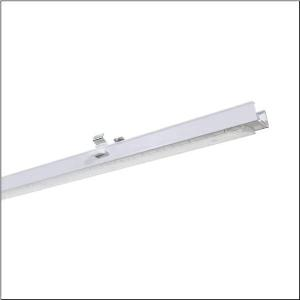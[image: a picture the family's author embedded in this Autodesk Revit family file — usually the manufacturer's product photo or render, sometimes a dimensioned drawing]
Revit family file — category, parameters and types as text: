
# Revit family: trunking_flex_31_51re19mb4cb
name_source: partatom
category: Lighting Fixtures
units: mm (PartAtom-declared; Revit-internal decimal feet)

## family parameters
Cut with Voids When Loaded = No
Host = Face
Light Source = No
Part Type = Normal
Room Calculation Point = No
Round Connector Dimension = Use Diameter
Shared = No

## types (1)
- --- (1 x LED, 11500 lm, 66 W, 4000K)
    Apparent Load = 66 VA
    CIE Flux Codes = 66 89 98 99 100
    Color Rendering = 80
    Color Temperature = 4000K
    Default Elevation = 1800 mm
    Description = Trunking Flex 31, luminaire insert, of extruded aluminium section, coated, traffic white (RAL 9016), length: 1.472mm, width: 91mm, height: 53mm, LED rated luminous flux: 11.500lm, light colour: 840, control gear: ON/OFF Multilumen, with system connector: socket, mains connection: 220..240V, AC, 50/60Hz, rated input power: 66W, connected load according to luminous flux setting (19/24/32/37/47/52/60/66W), luminous flux adjustable on luminaire in eight steps (3450/4380/5800/6700/8350/9200/10500/11500lm ), primary light control with lens, of plastic, primary optical cover: cover, of PMMA, light emission: direct distribution, primary light characteristic: double asymmetric, protection rating (complete): IP20, insulation class (complete): insulation class I (protective earthing), certification: CE, UKCA, impact resistance: IK02, permissible ambient temperature for indoor applications: -20..+40°C, packaging unit: 1 piece
    Height = 58 mm
    Lamp = 1 x LED
    Lamp Light Flux = 11500 lm
    Lamp Power = 66 W
    Lamp count = 1
    Length = 1472 mm
    Luminous efficacy = 174 lm/W
    Manufacturer = Siteco
    ModVariant = No
    Model = 51RE19MB4CB
    Mounting Place = Ceiling
    Mounting Type = Pendant
    Number of Poles = 1
    OnlyDefault = Yes
    Power Factor = 1
    Product Name = Trunking Flex 31
    Product group = luminaire insert
    ProductGroupID = 901
    Protection Class = Protection class I
    Protection Degree = IP 20
    RLX_Detail_Level = 1
    RLX_Emergency_Light_Flux = 0 lm
    RLX_Emergency_Type = 0
    RLX_Emergency_Type_DB = No
    RlxData = <blob elided: 21165 chars, md5=249072ce>
    Socket = socket
    Standby Power = 0 W
    System Light Flux = 11500 lm
    System Power = 66 W
    Type Comments = factory setting: luminous flux: 100 % | (ON | ON | ON)
    Type Image = l_1266702.jpg
    URL = http://relux.com
    VarID = @adj_001343
    Voltage = 0 V
    Weight = 0.00 kg
    Width = 65 mm

## geometry (parser evidence)
native form markers: Blend x4, Sweep x9
no freeform markers — native parametric forms only
